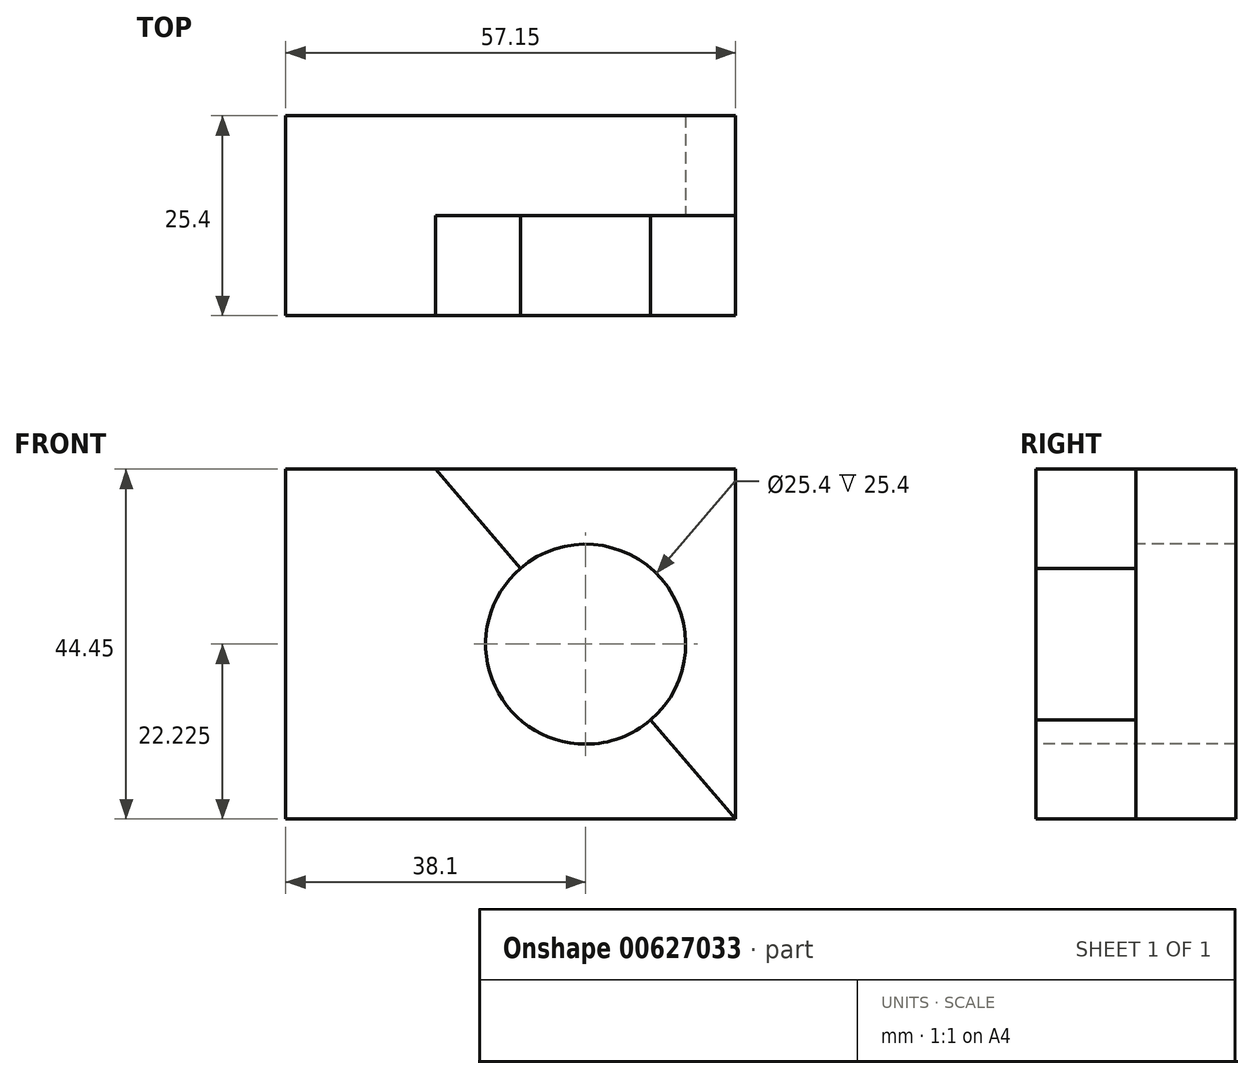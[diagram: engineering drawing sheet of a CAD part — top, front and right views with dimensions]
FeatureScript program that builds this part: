
annotation { "Feature Type Name" : "Feature", "Feature Type Description" : "" }
export const myFeature = defineFeature(function(context is Context, id is Id, definition is map)
    precondition{}
    {
        {
            var Q0;
            Q0=qCreatedBy(makeId("Right.planeOp"),FACE);
            var sketch = newSketch(context, id + "F0", { "sketchPlane" : qUnion([Q0])});
            skLineSegment(sketch, "E0", {"start": v(0, 0) * mm, "end": v(12.7, 0) * mm});
            skLineSegment(sketch, "E1", {"start": v(12.7, 0) * mm, "end": v(12.7, 44.45) * mm});
            skLineSegment(sketch, "E2", {"start": v(12.7, 44.45) * mm, "end": v(0, 44.45) * mm});
            skLineSegment(sketch, "E3", {"start": v(0, 44.45) * mm, "end": v(0, 0) * mm});
            skSolve(sketch);
        }
        {
            var Q0;
            Q0 = qSketchRegion(id + "F0", true);
            extrude(context, id + "F1", {"entities" : qUnion([Q0]), "depth" : 57.15 * mm, "offsetDistance" : 25.4 * mm});
        }
        {
            var Q0;
            Q0=makeQuery(id+"F1.opExtrude","SWEPT_FACE",FACE,{"disambiguationData":[OSD([sQuery(id+"F0.wireOp",EDGE,"E3")])]});
            var sketch = newSketch(context, id + "F2", { "sketchPlane" : qUnion([Q0])});
            skLineSegment(sketch, "E4", {"start": v(0, 0) * mm, "end": v(0, 44.45) * mm});
            skLineSegment(sketch, "E5", {"start": v(0, 44.45) * mm, "end": v(19.05, 44.45) * mm});
            skLineSegment(sketch, "E6", {"start": v(19.05, 44.45) * mm, "end": v(57.15, 0) * mm});
            skLineSegment(sketch, "E7", {"start": v(57.15, 0) * mm, "end": v(0, 0) * mm});
            skSolve(sketch);
        }
        {
            var Q0;
            Q0 = qSketchRegion(id + "F2", true);
            extrude(context, id + "F3", {"entities" : qUnion([Q0]), "operationType" : NewBodyOperationType.ADD, "depth" : 12.7 * mm, "offsetDistance" : 25.4 * mm});
        }
        {
            var Q0;
            Q0=makeQuery(id+"F3.opExtrude","CAP_FACE",FACE,{"disambiguationData":[OSD([sQuery(id+"F2.wireOp",EDGE,"E4"),sQuery(id+"F2.wireOp",EDGE,"E5"),sQuery(id+"F2.wireOp",EDGE,"E6"),sQuery(id+"F2.wireOp",EDGE,"E7")])],"isStart":false});
            var sketch = newSketch(context, id + "F4", { "sketchPlane" : qUnion([Q0])});
            skCircle(sketch, "E8", {"center": v(38.1, 22.22) * mm, "radius": 12.7 * mm});
            skSolve(sketch);
        }
        {
            var Q0;
            {var subQ0=sQuery(id+"F4.wireOp",EDGE,"E8");var subQ1=makeQuery(id+"F3.opExtrude","CAP_EDGE",EDGE,{"disambiguationData":[OSD([sQuery(id+"F2.wireOp",EDGE,"E6")])],"isStart":false});var subQ2=makeQuery(id+"F4.imprint","INTERSECT",VERTEX,{"disambiguationData":[OD(0.0)],"derivedFrom":[subQ1,subQ0]});Q0=makeQuery(id+"F4.imprint","IMPRINT",FACE,{"disambiguationData":[TD([[makeQuery(id+"F4.imprint","IMPRINT",EDGE,{"disambiguationData":[TD([[subQ2,-1.0]])],"derivedFrom":subQ0}),1.0]])]});}
            var Q1;
            {var subQ0=sQuery(id+"F4.wireOp",EDGE,"E8");var subQ1=makeQuery(id+"F3.opExtrude","CAP_EDGE",EDGE,{"disambiguationData":[OSD([sQuery(id+"F2.wireOp",EDGE,"E6")])],"isStart":false});var subQ2=makeQuery(id+"F4.imprint","INTERSECT",VERTEX,{"disambiguationData":[OD(0.0)],"derivedFrom":[subQ1,subQ0]});Q1=makeQuery(id+"F4.imprint","IMPRINT",FACE,{"disambiguationData":[TD([[makeQuery(id+"F4.imprint","IMPRINT",EDGE,{"disambiguationData":[TD([[subQ2,1.0]])],"derivedFrom":subQ0}),1.0]])]});}
            extrude(context, id + "F5", {"entities" : qUnion([Q0, Q1]), "operationType" : NewBodyOperationType.REMOVE, "oppositeDirection" : true, "depth" : 25.4 * mm, "offsetDistance" : 25.4 * mm});
        }
    });
